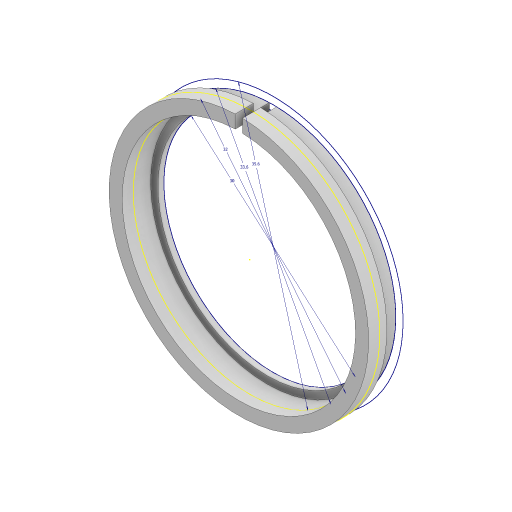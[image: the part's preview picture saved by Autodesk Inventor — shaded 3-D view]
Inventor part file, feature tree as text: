
AUTODESK INVENTOR PART (.ipt)
format: ipt  version: 2023 (Build 270158000, 158)  size: 164,352 bytes
history: native  units: mm
features: extrude x5, sketch x3
ambient origin geometry x8: Origin, YZ Plane, XZ Plane, XY Plane, X Axis, Y Axis, Z Axis, Center Point
bodies: Solid1 (feature_tree)
feature tree (8):
  sketch  "Sketch1"  dims[d0=33.6mm d1=30.0mm]
  extrude  "Extrusion1"  Depth=30.0mm
  extrude  "Extrusion2"  Depth=32.0mm
  sketch  "Sketch2"  dims[d2=35.6mm d3=32.0mm]
  extrude  "Extrusion3"  Depth=3.2mm TaperAngle=0.0deg
  extrude  "Extrusion5"  Depth=1.0mm TaperAngle=0.0deg
  extrude  "Extrusion4"  Depth=1.0mm
  sketch  "Sketch3"  dims[d4=0.8mm d5=0.0mm d6=3.2mm d7=0.0mm d8=1.5mm d9=0.0mm d10=1.0mm d11=16.0mm d12=10.0mm d13=0.0mm d14=1.0mm d15=0.0mm d16=0.5mm d17=0.872665mm d18=0.5mm d19=0.872665mm]
